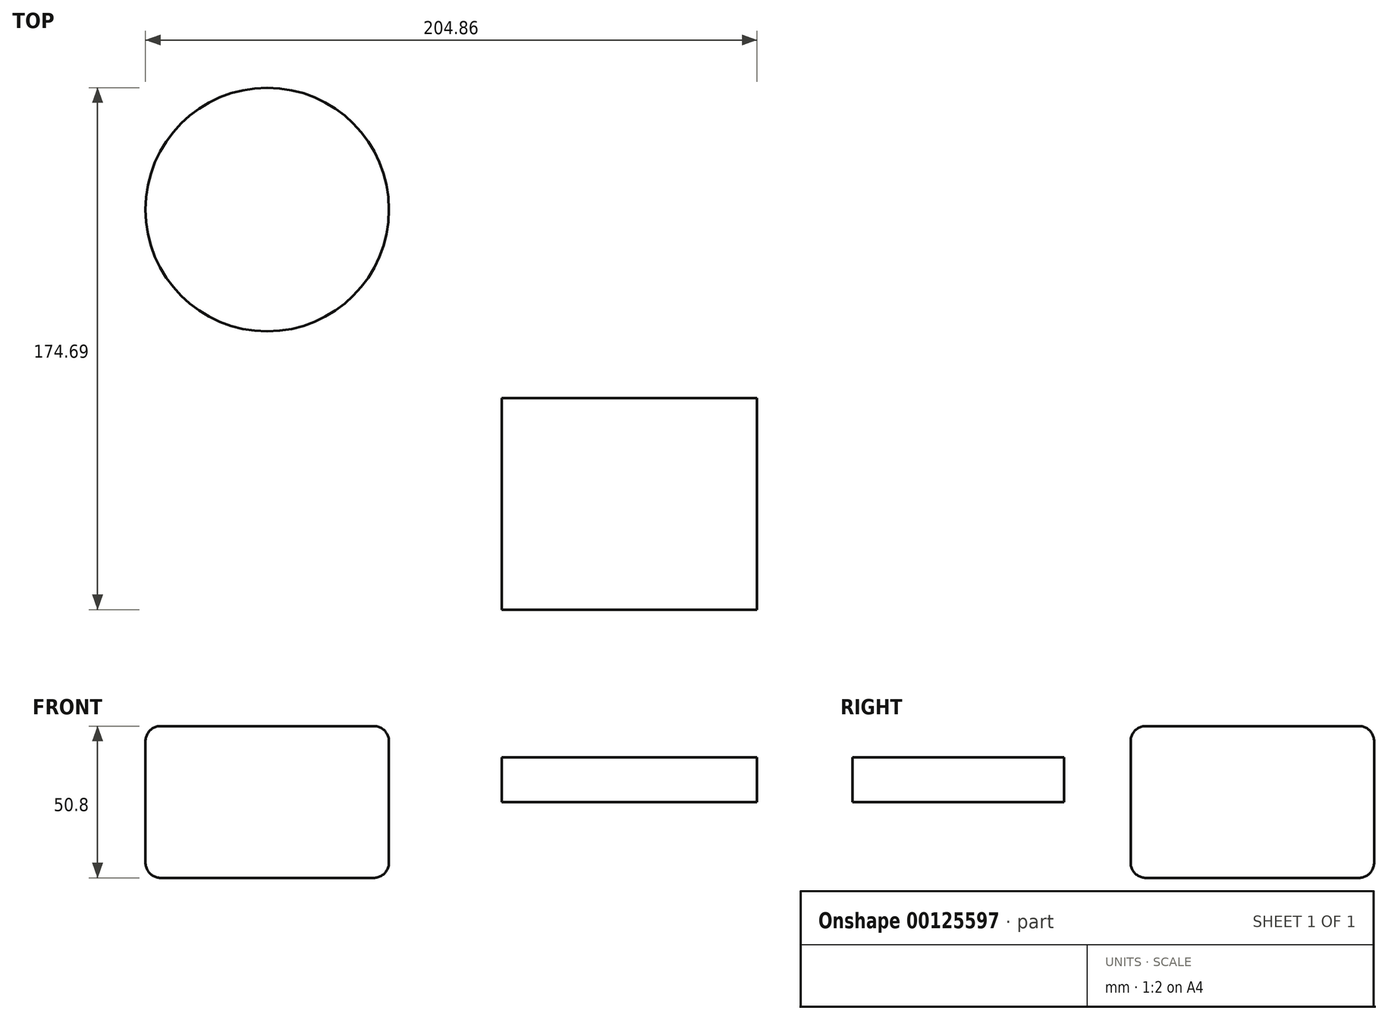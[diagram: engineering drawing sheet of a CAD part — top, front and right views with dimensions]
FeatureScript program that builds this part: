
annotation { "Feature Type Name" : "Feature", "Feature Type Description" : "" }
export const myFeature = defineFeature(function(context is Context, id is Id, definition is map)
    precondition{}
    {
        {
            var Q0;
            Q0=qCreatedBy(makeId("Top.planeOp"),FACE);
            var sketch = newSketch(context, id + "F0", { "sketchPlane" : qUnion([Q0])});
            skCircle(sketch, "E0", {"center": v(-11.26, 18) * mm, "radius": 40.77 * mm});
            skSolve(sketch);
        }
        {
            var Q0;
            Q0=makeQuery(id+"F0.imprint","IMPRINT",FACE,{"disambiguationData":[TD([[makeQuery(id+"F0.imprint","IMPRINT",EDGE,{"derivedFrom":sQuery(id+"F0.wireOp",EDGE,"E0")}),1.0]])]});
            extrude(context, id + "F1", {"entities" : qUnion([Q0]), "depth" : 25.4 * mm});
        }
        {
            var Q0;
            Q0=makeQuery(id+"F1.opExtrude","SWEPT_BODY",BODY,{"disambiguationData":[OSD([sQuery(id+"F0.wireOp",EDGE,"E0")])]});
            var Q1;
            Q1=makeQuery(id+"F1.opExtrude","SWEPT_FACE",FACE,{"disambiguationData":[OSD([sQuery(id+"F0.wireOp",EDGE,"E0")])]});
            var Q2;
            Q2=makeQuery(id+"F1.opExtrude","CAP_FACE",FACE,{"disambiguationData":[OSD([sQuery(id+"F0.wireOp",EDGE,"E0")])],"isStart":false});
            var Q3;
            Q3=qCreatedBy(makeId("Top.planeOp"),FACE);
            mirror(context, id + "F2", {"operationType" : NewBodyOperationType.ADD, "entities" : qUnion([Q0]), "faces" : qUnion([Q1, Q2]), "mirrorPlane" : qUnion([Q3])});
        }
        {
            var Q0;
            Q0=makeQuery(id+"F1.opExtrude","CAP_EDGE",EDGE,{"disambiguationData":[OSD([sQuery(id+"F0.wireOp",EDGE,"E0")])],"isStart":false});
            fillet(context, id + "F3", {"entities" : qUnion([Q0]), "radius" : 5.08 * mm, "tangentPropagation" : true, "allowEdgeOverflow" : false});
        }
        {
            var Q0;
            Q0=makeQuery(id+"F2.opPattern","COPY",EDGE,{"derivedFrom":makeQuery(id+"F1.opExtrude","CAP_EDGE",EDGE,{"disambiguationData":[OSD([sQuery(id+"F0.wireOp",EDGE,"E0")])],"isStart":false}),"instanceName":"1"});
            fillet(context, id + "F4", {"entities" : qUnion([Q0]), "radius" : 5.08 * mm, "tangentPropagation" : true, "allowEdgeOverflow" : false});
        }
        {
            var Q0;
            Q0=makeQuery(id+"F2.opPattern","COPY",FACE,{"derivedFrom":makeQuery(id+"F1.opExtrude","CAP_FACE",FACE,{"disambiguationData":[OSD([sQuery(id+"F0.wireOp",EDGE,"E0")])],"isStart":false}),"instanceName":"1"});
            var sketch = newSketch(context, id + "F5", { "sketchPlane" : qUnion([Q0])});
            skCircle(sketch, "E1", {"center": v(-11.26, -18) * mm, "radius": 32.48 * mm});
            skSolve(sketch);
        }
        {
            var Q0;
            Q0=makeQuery(id+"F5.imprint","IMPRINT",FACE,{"disambiguationData":[TD([[makeQuery(id+"F5.imprint","IMPRINT",EDGE,{"derivedFrom":sQuery(id+"F5.wireOp",EDGE,"E1")}),1.0]])]});
            var sketch = newSketch(context, id + "F6", { "sketchPlane" : qUnion([Q0])});
            skSolve(sketch);
        }
        {
            var Q0;
            Q0=qCreatedBy(makeId("Top.planeOp"),FACE);
            var sketch = newSketch(context, id + "F7", { "sketchPlane" : qUnion([Q0])});
            skLineSegment(sketch, "E2.bottom", {"start": v(67.3, -115.92) * mm, "end": v(152.82, -115.92) * mm});
            skLineSegment(sketch, "E2.top", {"start": v(67.3, -45.12) * mm, "end": v(152.82, -45.12) * mm});
            skLineSegment(sketch, "E2.left", {"start": v(67.3, -115.92) * mm, "end": v(67.3, -45.12) * mm});
            skLineSegment(sketch, "E2.right", {"start": v(152.82, -115.92) * mm, "end": v(152.82, -45.12) * mm});
            skSolve(sketch);
        }
        {
            var Q0;
            Q0=makeQuery(id+"F7.imprint","IMPRINT",FACE,{"disambiguationData":[TD([[makeQuery(id+"F7.imprint","IMPRINT",EDGE,{"derivedFrom":sQuery(id+"F7.wireOp",EDGE,"E2.bottom")}),1.0]])]});
            extrude(context, id + "F8", {"entities" : qUnion([Q0]), "depth" : 15 * mm, "offsetDistance" : 25.4 * mm});
        }
    });
